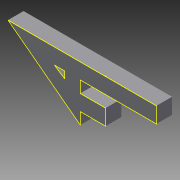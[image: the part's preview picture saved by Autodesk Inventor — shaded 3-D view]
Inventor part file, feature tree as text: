
AUTODESK INVENTOR PART (.ipt)
format: ipt  version: 2013 (Build 170138000, 138)  size: 120,832 bytes
history: native  units: in
note: dims shown in document units (in); Inventor stores cm internally (conversion verified against a paired STEP export)
features: sketch x3, extrude x2
ambient origin geometry x8: Origin, YZ Plane, XZ Plane, XY Plane, X Axis, Y Axis, Z Axis, Center Point
feature tree (5):
  extrude  "Extrusion2"  Depth=3.5in
  extrude  "Extrusion3"  Depth=0.75in
  sketch  "Sketch5"  dims[d5=1.0in d6=1.0in d7=1.0in d8=1.0in d9=3.5in d12=1.0in d13=9.75in d14=1.0in d15=0.0in d16=3.25in d17=1.0in d18=0.0in d19=0.9818in d20=0.255in d21=0.3634in d22=5.8001in d23=1.6572in]
  sketch  "Sketch1"  dims[d0=6.25in d1=3.5in]
  sketch  "Sketch4"  dims[d2=1.625in d3=0.75in]
